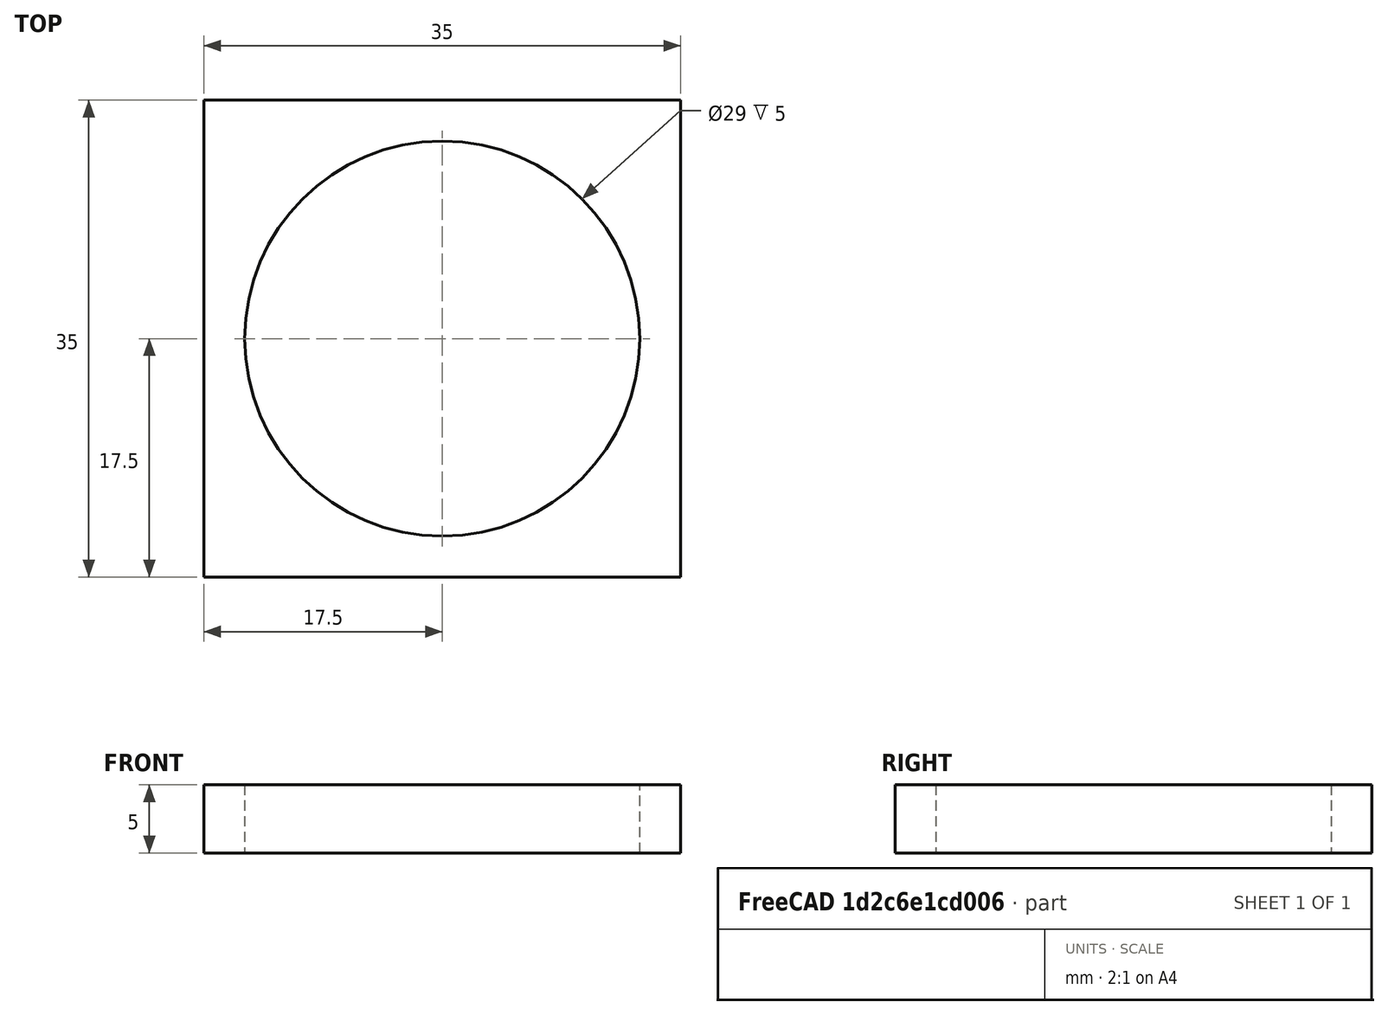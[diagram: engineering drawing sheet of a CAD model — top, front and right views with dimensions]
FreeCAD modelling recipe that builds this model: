
FCSTD DOCUMENT
Label: cup_holder
objects: Sketcher::SketchObject×1, PartDesign::Pad×1
note: 3 computed .brp shape members not serialized (recipe doc carries the construction recipe); baked Part::Feature solids carry a one-line shape summary decoded from their .brp

FEATURE [Sketcher::SketchObject] Sketch
  sketch-geometry (5):
    g0: LineSegment StartX=0 StartY=0 StartZ=0 EndX=35 EndY=0 EndZ=0
    g1: LineSegment StartX=35 StartY=0 StartZ=0 EndX=35 EndY=35 EndZ=0
    g2: LineSegment StartX=35 StartY=35 StartZ=0 EndX=0 EndY=35 EndZ=0
    g3: LineSegment StartX=0 StartY=35 StartZ=0 EndX=0 EndY=0 EndZ=0
    g4: Circle CenterX=17.5 CenterY=17.5 CenterZ=0 NormalX=0 NormalY=0 NormalZ=1 Radius=14.5
  constraints (14):
    c: Coincident(g0,g1)
    c: Coincident(g1,g2)
    c: Coincident(g2,g3)
    c: Coincident(g3,g0)
    c: Horizontal(g0)
    c: Horizontal(g2)
    c: Vertical(g1)
    c: Vertical(g3)
    c: Coincident(g0,g-1)
    c: DistanceX(g2) = -35
    c: DistanceY(g1) = 35
    c: Radius(g4) = 14.5
    c: DistanceY(g4,g1) = 17.5
    c: DistanceX(g4,g1) = 17.5
FEATURE [PartDesign::Pad] Pad
  Length = 5
  Length2 = 100
  Sketch = -> Sketch
  Type = 0
